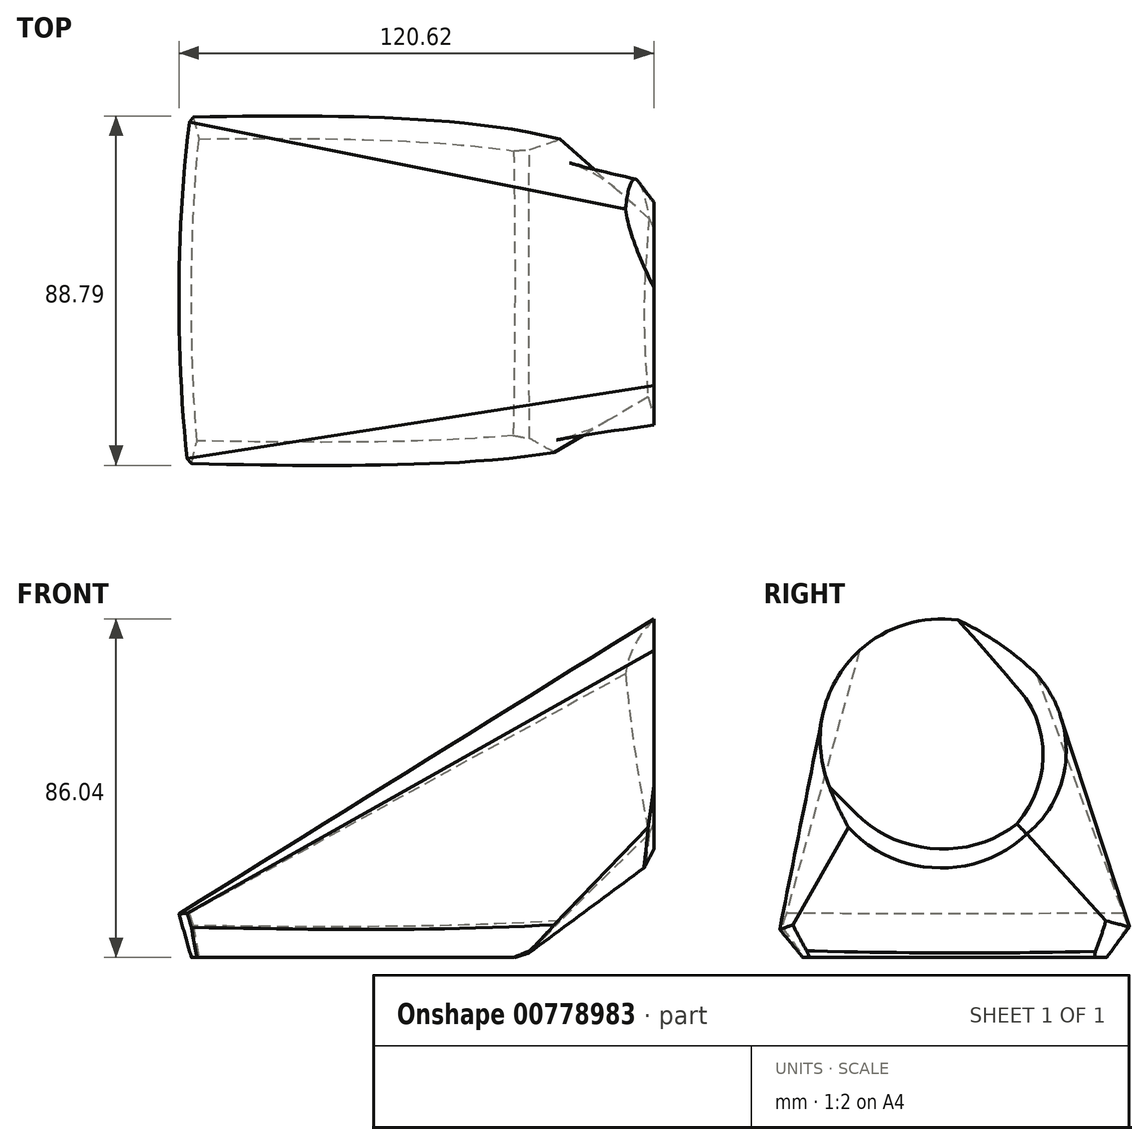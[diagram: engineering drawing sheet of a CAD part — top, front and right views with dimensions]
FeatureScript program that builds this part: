
annotation { "Feature Type Name" : "Feature", "Feature Type Description" : "" }
export const myFeature = defineFeature(function(context is Context, id is Id, definition is map)
    precondition{}
    {
        {
            var Q0;
            Q0=qCreatedBy(makeId("Top.planeOp"),FACE);
            var sketch = newSketch(context, id + "F0", { "sketchPlane" : qUnion([Q0])});
            skLineSegment(sketch, "E0.bottom", {"start": v(-138.48, 44.57) * mm, "end": v(-33.33, 44.57) * mm});
            skLineSegment(sketch, "E0.top", {"start": v(-138.48, -48.22) * mm, "end": v(-33.33, -48.22) * mm});
            skLineSegment(sketch, "E0.left", {"start": v(-138.48, 44.57) * mm, "end": v(-138.48, -48.22) * mm});
            skLineSegment(sketch, "E0.right", {"start": v(-33.33, 44.57) * mm, "end": v(-33.33, -48.22) * mm});
            skSolve(sketch);
        }
        {
            var Q0;
            Q0=qCreatedBy(makeId("Right.planeOp"),FACE);
            var sketch = newSketch(context, id + "F1", { "sketchPlane" : qUnion([Q0])});
            skCircle(sketch, "E1", {"center": v(-5.79, 55.31) * mm, "radius": 30.73 * mm});
            skSolve(sketch);
        }
        {
            var Q0;
            Q0=makeQuery(id+"F1.imprint","IMPRINT",FACE,{"disambiguationData":[TD([[makeQuery(id+"F1.imprint","IMPRINT",EDGE,{"derivedFrom":sQuery(id+"F1.wireOp",EDGE,"E1")}),1.0]])]});
            var Q1;
            Q1=makeQuery(id+"F0.imprint","IMPRINT",FACE,{"disambiguationData":[TD([[makeQuery(id+"F0.imprint","IMPRINT",EDGE,{"derivedFrom":sQuery(id+"F0.wireOp",EDGE,"E0.bottom")}),-1.0]])]});
            loft(context, id + "F2", {"sheetProfilesArray" : [{ "sheetProfileEntities" : qUnion([Q0]) }, { "sheetProfileEntities" : qUnion([Q1]) }]});
        }
        {
            var Q0;
            Q0=makeQuery(id+"F2.opLoft","MID_CAP_EDGE",EDGE,{"disambiguationData":[OSD([sQuery(id+"F0.wireOp",EDGE,"E0.bottom"),sQuery(id+"F0.wireOp",EDGE,"E0.left"),sQuery(id+"F0.wireOp",EDGE,"E0.right")])],"capPos":1.0});
            var Q1;
            Q1=makeQuery(id+"F2.opLoft","MID_CAP_EDGE",EDGE,{"disambiguationData":[OSD([sQuery(id+"F0.wireOp",EDGE,"E0.bottom"),sQuery(id+"F0.wireOp",EDGE,"E0.top"),sQuery(id+"F0.wireOp",EDGE,"E0.right")])],"capPos":1.0});
            var Q2;
            Q2=makeQuery(id+"F2.opLoft","MID_CAP_EDGE",EDGE,{"disambiguationData":[OSD([sQuery(id+"F0.wireOp",EDGE,"E0.bottom"),sQuery(id+"F0.wireOp",EDGE,"E0.top"),sQuery(id+"F0.wireOp",EDGE,"E0.left")])],"capPos":1.0});
            var Q3;
            Q3=makeQuery(id+"F2.opLoft","MID_CAP_EDGE",EDGE,{"disambiguationData":[OSD([sQuery(id+"F0.wireOp",EDGE,"E0.top"),sQuery(id+"F0.wireOp",EDGE,"E0.left"),sQuery(id+"F0.wireOp",EDGE,"E0.right")])],"capPos":1.0});
            var Q4;
            Q4=makeQuery(id+"F2.opLoft","MID_CAP_EDGE",EDGE,{"disambiguationData":[OSD([sQuery(id+"F0.wireOp",EDGE,"E0.bottom"),sQuery(id+"F0.wireOp",EDGE,"E0.top"),sQuery(id+"F0.wireOp",EDGE,"E0.left"),sQuery(id+"F1.wireOp",EDGE,"E1")])],"capPos":0.0});
            var Q5;
            Q5=makeQuery(id+"F2.opLoft","MID_CAP_EDGE",EDGE,{"disambiguationData":[OSD([sQuery(id+"F0.wireOp",EDGE,"E0.top"),sQuery(id+"F0.wireOp",EDGE,"E0.left"),sQuery(id+"F0.wireOp",EDGE,"E0.right"),sQuery(id+"F1.wireOp",EDGE,"E1")])],"capPos":0.0});
            var Q6;
            Q6=makeQuery(id+"F2.opLoft","MID_CAP_EDGE",EDGE,{"disambiguationData":[OSD([sQuery(id+"F0.wireOp",EDGE,"E0.bottom"),sQuery(id+"F0.wireOp",EDGE,"E0.left"),sQuery(id+"F0.wireOp",EDGE,"E0.right"),sQuery(id+"F1.wireOp",EDGE,"E1")])],"capPos":0.0});
            var Q7;
            Q7=makeQuery(id+"F2.opLoft","MID_CAP_EDGE",EDGE,{"disambiguationData":[OSD([sQuery(id+"F0.wireOp",EDGE,"E0.bottom"),sQuery(id+"F0.wireOp",EDGE,"E0.top"),sQuery(id+"F0.wireOp",EDGE,"E0.right"),sQuery(id+"F1.wireOp",EDGE,"E1")])],"capPos":0.0});
            chamfer(context, id + "F3", {"entities" : qUnion([Q0, Q1, Q2, Q3, Q4, Q5, Q6, Q7]), "width" : 6 * mm, "tangentPropagation" : true});
        }
    });
